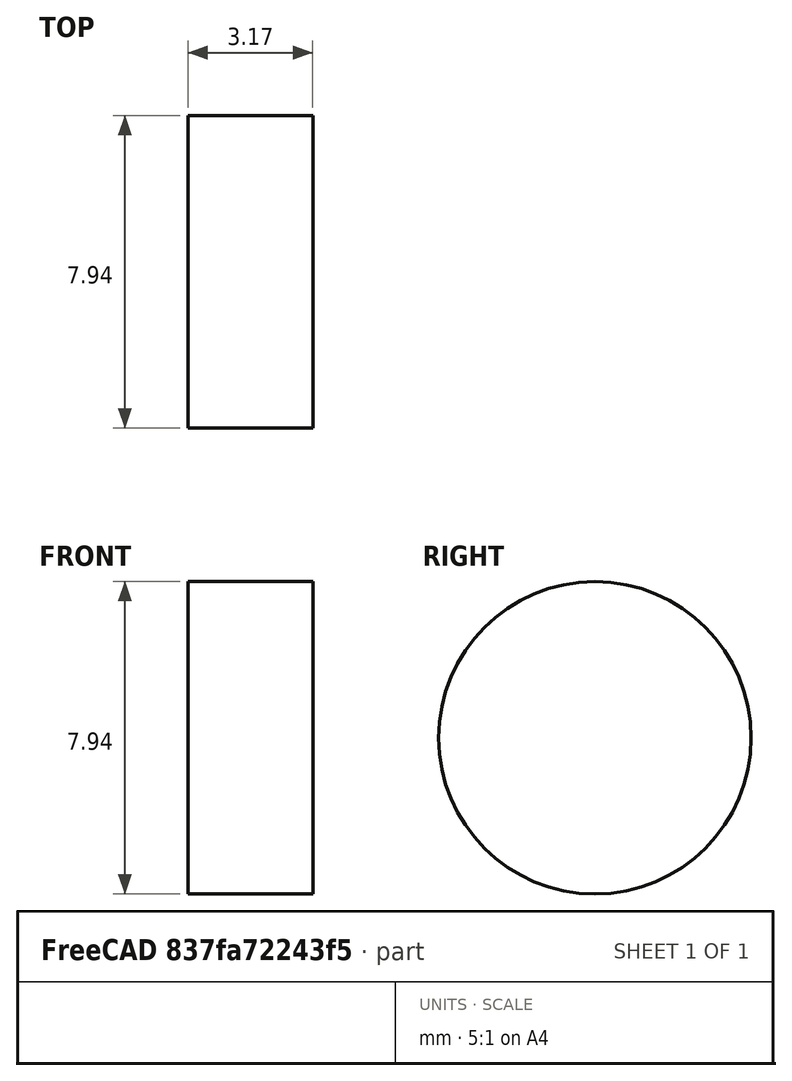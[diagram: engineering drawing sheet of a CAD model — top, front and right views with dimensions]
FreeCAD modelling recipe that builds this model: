
FCSTD DOCUMENT  (FreeCAD 2023.521R14555 (Git shallow))
Label: Magnet
License: All rights reserved
LicenseURL: http://en.wikipedia.org/wiki/All_rights_reserved
objects: Sketcher::SketchObject×1, PartDesign::Pad×1, PartDesign::CoordinateSystem×1, PartDesign::Body×1
note: 7 computed .brp shape members not serialized (recipe doc carries the construction recipe); baked Part::Feature solids carry a one-line shape summary decoded from their .brp

FEATURE [Sketcher::SketchObject] Sketch
  ArcFitTolerance = 0
  AttachmentSupport = -> [YZ_Plane]
  ExternalBSplineMaxDegree = 0
  ExternalBSplineTolerance = 0
  FullyConstrained = true
  InternalTolerance = 1e-06
  InvalidShape = false
  MakeInternals = false
  MapMode = 5
  Placement = pos=(0,0,0) rot=(0.57735,0.57735,0.57735;2.0944rad)
  Support = -> [YZ_Plane]
  TreeRank = 0
  ValidateShape = false
  sketch-geometry (1):
    g0: Circle CenterX=0 CenterY=0 CenterZ=0 NormalX=0 NormalY=0 NormalZ=1 AngleXU=0 Radius=3.96875
  constraints (2):
    c: Coincident(g0,g-1)
    c: Diameter(g0) = 7.9375
FEATURE [PartDesign::Pad] Pad
  AddSubType = 0
  AutoTaperInnerAngle = true
  CheckUpToFaceLimits = true
  ClaimChildren = false
  Direction = (1,-2e-16,3e-16)
  Fit = 0
  FitJoin = 0
  InnerFit = 0
  InnerFitJoin = 0
  InvalidShape = false
  Length = 3.175
  Length2 = 10
  NewSolid = false
  Profile = -> Sketch
  ReferenceAxis = -> Sketch [N_Axis]
  Suppress = false
  TaperInnerAngle = 0
  TaperInnerAngleRev = 0
  TreeRank = 0
  Type = 0
  ValidateShape = true
  _ProfileBasedVersion = 0
FEATURE [PartDesign::CoordinateSystem] LCS_1
  AttacherType = Attacher::AttachEngine3D
  AttachmentSupport = -> [Pad]
  InvalidShape = false
  MapMode = 45
  Placement = pos=(3.175,-1.1e-15,1e-15) rot=(0.57735,0.57735,0.57735;2.0944rad)
  Support = -> [Pad]
  TreeRank = 0
  ValidateShape = false
FEATURE [PartDesign::Body] Body  label="Magnet"
  AutoGroupSolids = false
  ClaimAllChildren = false
  ExportMode = 0
  Group = -> [Sketch,Pad,LCS_1]
  InvalidShape = false
  Origin = -> Origin
  Tip = -> Pad
  TreeRank = 0
  ValidateShape = false
  _ExportChildren = -> [Pad,LCS_1]
  _GroupVersion = 1
